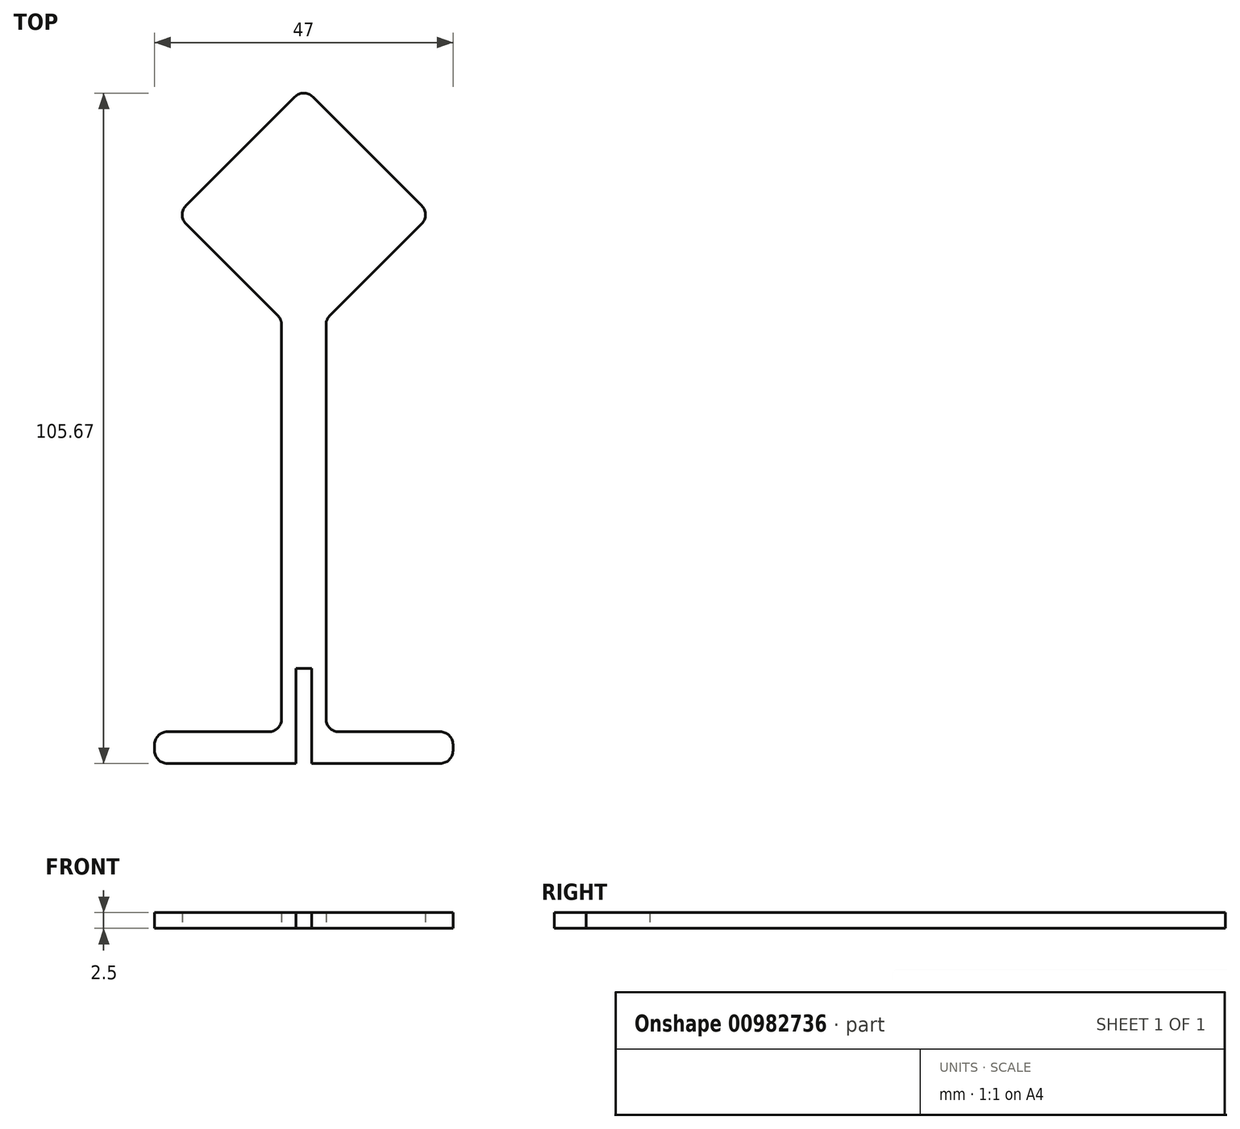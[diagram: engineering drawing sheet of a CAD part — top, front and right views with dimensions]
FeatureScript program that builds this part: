
annotation { "Feature Type Name" : "Feature", "Feature Type Description" : "" }
export const myFeature = defineFeature(function(context is Context, id is Id, definition is map)
    precondition{}
    {
        {
            var Q0;
            Q0=qCreatedBy(makeId("Top.planeOp"),FACE);
            var sketch = newSketch(context, id + "F0", { "sketchPlane" : qUnion([Q0])});
            skLineSegment(sketch, "E0", {"start": v(-3.5, -0.5) * mm, "end": v(-3.5, -65.5) * mm});
            skLineSegment(sketch, "E1", {"start": v(-3.5, -65.5) * mm, "end": v(-23.5, -65.5) * mm});
            skLineSegment(sketch, "E2", {"start": v(-23.5, -65.5) * mm, "end": v(-23.5, -70.5) * mm});
            skLineSegment(sketch, "E3", {"start": v(-23.5, -70.5) * mm, "end": v(23.5, -70.5) * mm});
            skLineSegment(sketch, "E4", {"start": v(23.5, -70.5) * mm, "end": v(23.5, -65.5) * mm});
            skLineSegment(sketch, "E5", {"start": v(23.5, -65.5) * mm, "end": v(3.5, -65.5) * mm});
            skLineSegment(sketch, "E6", {"start": v(3.5, -65.5) * mm, "end": v(3.5, -0.5) * mm});
            skLineSegment(sketch, "E7.bottom", {"start": v(1.25, -70.5) * mm, "end": v(-1.25, -70.5) * mm});
            skLineSegment(sketch, "E7.top", {"start": v(1.25, -55.5) * mm, "end": v(-1.25, -55.5) * mm});
            skLineSegment(sketch, "E7.left", {"start": v(1.25, -70.5) * mm, "end": v(1.25, -55.5) * mm});
            skLineSegment(sketch, "E7.right", {"start": v(-1.25, -70.5) * mm, "end": v(-1.25, -55.5) * mm});
            skPoint(sketch, "E7.middle", {"position": v(0, -63) * mm});
            skLineSegment(sketch, "E8.bottom", {"start": v(-23.5, -70.5) * mm, "end": v(-17.5, -70.5) * mm});
            skLineSegment(sketch, "E8.top", {"start": v(-23.5, -70.8) * mm, "end": v(-17.5, -70.8) * mm});
            skLineSegment(sketch, "E8.left", {"start": v(-23.5, -70.5) * mm, "end": v(-23.5, -70.8) * mm});
            skLineSegment(sketch, "E8.right", {"start": v(-17.5, -70.5) * mm, "end": v(-17.5, -70.8) * mm});
            skLineSegment(sketch, "E9.MirrorCS", {"start": v(23.5, -70.5) * mm, "end": v(17.5, -70.5) * mm});
            skLineSegment(sketch, "E10.MirrorCS", {"start": v(17.5, -70.5) * mm, "end": v(17.5, -70.8) * mm});
            skLineSegment(sketch, "E11.MirrorCS", {"start": v(23.5, -70.8) * mm, "end": v(17.5, -70.8) * mm});
            skLineSegment(sketch, "E12.MirrorCS", {"start": v(23.5, -70.5) * mm, "end": v(23.5, -70.8) * mm});
            skLineSegment(sketch, "E13", {"start": v(0, 36) * mm, "end": v(-20, 16) * mm});
            skLineSegment(sketch, "E14", {"start": v(-20, 16) * mm, "end": v(0, -4) * mm});
            skLineSegment(sketch, "E15", {"start": v(0, -4) * mm, "end": v(20, 16) * mm});
            skLineSegment(sketch, "E16", {"start": v(20, 16) * mm, "end": v(0, 36) * mm});
            skSolve(sketch);
        }
        {
            var Q0;
            {var subQ0=sQuery(id+"F0.wireOp",EDGE,"im0v1Rov-prSM-cwdN-f0IW-ScqFdnQkXUSi");Q0=makeQuery(id+"F0.imprint","IMPRINT",FACE,{"disambiguationData":[TD([[makeQuery(id+"F0.imprint","IMPRINT",EDGE,{"derivedFrom":subQ0}),1.0]])]});}
            var Q1;
            {var subQ7=sQuery(id+"F0.wireOp",EDGE,"E0");Q1=makeQuery(id+"F0.imprint","IMPRINT",FACE,{"disambiguationData":[TD([[makeQuery(id+"F0.imprint","IMPRINT",EDGE,{"derivedFrom":subQ7}),1.0]])]});}
            var Q2;
            Q2=makeQuery(id+"F0.imprint","IMPRINT",FACE,{"disambiguationData":[TD([[makeQuery(id+"F0.imprint","IMPRINT",EDGE,{"derivedFrom":sQuery(id+"F0.wireOp",EDGE,"E8.bottom")}),-1.0]])]});
            var Q3;
            Q3=makeQuery(id+"F0.imprint","IMPRINT",FACE,{"disambiguationData":[TD([[makeQuery(id+"F0.imprint","IMPRINT",EDGE,{"derivedFrom":sQuery(id+"F0.wireOp",EDGE,"E9.MirrorCS")}),1.0]])]});
            var Q4;
            {var subQ5=sQuery(id+"F0.wireOp",EDGE,"E13");Q4=makeQuery(id+"F0.imprint","IMPRINT",FACE,{"disambiguationData":[TD([[makeQuery(id+"F0.imprint","IMPRINT",EDGE,{"derivedFrom":subQ5}),1.0]])]});}
            extrude(context, id + "F1", {"entities" : qUnion([Q0, Q1, Q2, Q3, Q4]), "flatOperationType" : FlatOperationType.REMOVE, "depth" : 2.5 * mm, "offsetDistance" : 25 * mm, "domain" : OperationDomain.MODEL});
        }
        {
            var Q0;
            Q0=makeQuery(id+"F1.opExtrude","SWEPT_EDGE",EDGE,{"disambiguationData":[OSD([sQuery(id+"F0.wireOp",EDGE,"0U4RxweM-u2bA-2Qqt-OOBg-x1ftkZs6jUrD"),sQuery(id+"F0.wireOp",EDGE,"E0")])]});
            var Q1;
            Q1=makeQuery(id+"F1.opExtrude","SWEPT_EDGE",EDGE,{"disambiguationData":[OSD([sQuery(id+"F0.wireOp",EDGE,"0U4RxweM-u2bA-2Qqt-OOBg-x1ftkZs6jUrD"),sQuery(id+"F0.wireOp",EDGE,"E6")])]});
            var Q2;
            Q2=makeQuery(id+"F1.opExtrude","SWEPT_EDGE",EDGE,{"disambiguationData":[OSD([sQuery(id+"F0.wireOp",EDGE,"0U4RxweM-u2bA-2Qqt-OOBg-x1ftkZs6jUrD"),sQuery(id+"F0.wireOp",EDGE,"im0v1Rov-prSM-cwdN-f0IW-ScqFdnQkXUSi")])]});
            var Q3;
            Q3=makeQuery(id+"F1.opExtrude","SWEPT_EDGE",EDGE,{"disambiguationData":[OSD([sQuery(id+"F0.wireOp",EDGE,"0U4RxweM-u2bA-2Qqt-OOBg-x1ftkZs6jUrD"),sQuery(id+"F0.wireOp",EDGE,"IfBi3EXo-PReU-dRJG-joro-0UU4bWJMkuGZ")])]});
            var Q4;
            Q4=makeQuery(id+"F1.opExtrude","SWEPT_EDGE",EDGE,{"disambiguationData":[OSD([sQuery(id+"F0.wireOp",EDGE,"im0v1Rov-prSM-cwdN-f0IW-ScqFdnQkXUSi"),sQuery(id+"F0.wireOp",EDGE,"IfBi3EXo-PReU-dRJG-joro-0UU4bWJMkuGZ")])]});
            var Q5;
            Q5=makeQuery(id+"F1.opExtrude","SWEPT_EDGE",EDGE,{"disambiguationData":[OSD([sQuery(id+"F0.wireOp",EDGE,"E5"),sQuery(id+"F0.wireOp",EDGE,"E6")])]});
            var Q6;
            Q6=makeQuery(id+"F1.opExtrude","SWEPT_EDGE",EDGE,{"disambiguationData":[OSD([sQuery(id+"F0.wireOp",EDGE,"E0"),sQuery(id+"F0.wireOp",EDGE,"E1")])]});
            var Q7;
            Q7=makeQuery(id+"F1.opExtrude","SWEPT_EDGE",EDGE,{"disambiguationData":[OSD([sQuery(id+"F0.wireOp",EDGE,"E1"),sQuery(id+"F0.wireOp",EDGE,"E2")])]});
            var Q8;
            Q8=makeQuery(id+"F1.opExtrude","SWEPT_EDGE",EDGE,{"disambiguationData":[OSD([sQuery(id+"F0.wireOp",EDGE,"E4"),sQuery(id+"F0.wireOp",EDGE,"E5")])]});
            var Q9;
            Q9=makeQuery(id+"F1.opExtrude","SWEPT_EDGE",EDGE,{"disambiguationData":[OSD([sQuery(id+"F0.wireOp",EDGE,"E8.top"),sQuery(id+"F0.wireOp",EDGE,"E8.left")])]});
            var Q10;
            Q10=makeQuery(id+"F1.opExtrude","SWEPT_EDGE",EDGE,{"disambiguationData":[OSD([sQuery(id+"F0.wireOp",EDGE,"E11.MirrorCS"),sQuery(id+"F0.wireOp",EDGE,"E12.MirrorCS")])]});
            var Q11;
            Q11=makeQuery(id+"F1.opExtrude","SWEPT_EDGE",EDGE,{"disambiguationData":[OSD([sQuery(id+"F0.wireOp",EDGE,"E15"),sQuery(id+"F0.wireOp",EDGE,"E16")])]});
            var Q12;
            Q12=makeQuery(id+"F1.opExtrude","SWEPT_EDGE",EDGE,{"disambiguationData":[OSD([sQuery(id+"F0.wireOp",EDGE,"E13"),sQuery(id+"F0.wireOp",EDGE,"E16")])]});
            var Q13;
            Q13=makeQuery(id+"F1.opExtrude","SWEPT_EDGE",EDGE,{"disambiguationData":[OSD([sQuery(id+"F0.wireOp",EDGE,"E13"),sQuery(id+"F0.wireOp",EDGE,"E14")])]});
            fillet(context, id + "F2", {"entities" : qUnion([Q0, Q1, Q2, Q3, Q4, Q5, Q6, Q7, Q8, Q9, Q10, Q11, Q12, Q13]), "radius" : 2 * mm, "tangentPropagation" : true, "allowEdgeOverflow" : false});
        }
    });
